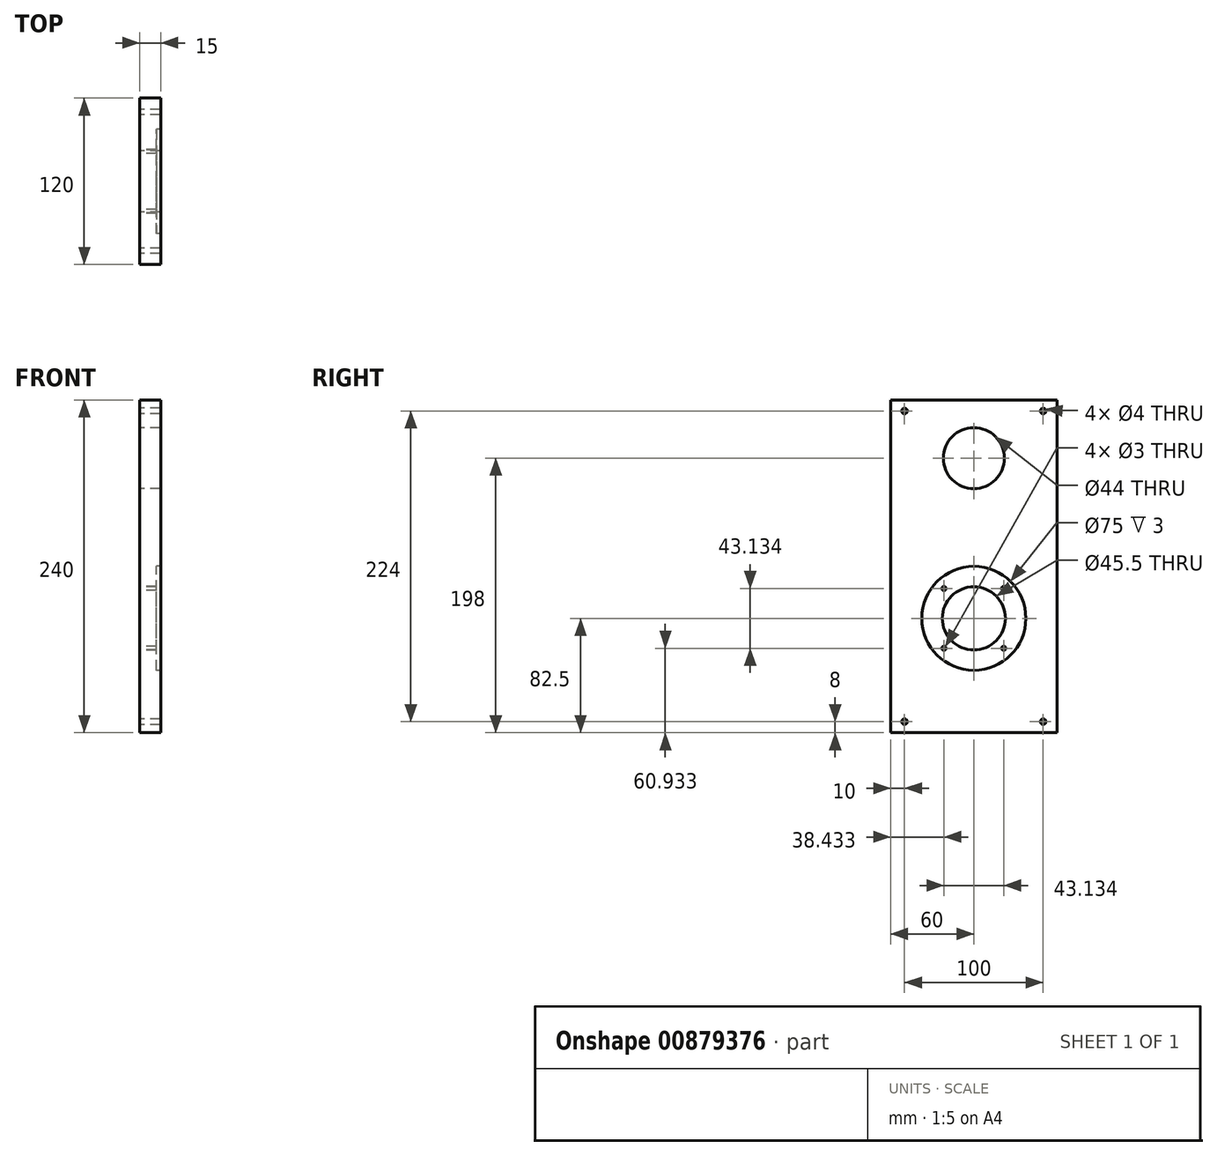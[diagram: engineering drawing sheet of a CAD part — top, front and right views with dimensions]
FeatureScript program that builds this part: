
annotation { "Feature Type Name" : "Feature", "Feature Type Description" : "" }
export const myFeature = defineFeature(function(context is Context, id is Id, definition is map)
    precondition{}
    {
        {
            var Q0;
            Q0=qCreatedBy(makeId("Right.planeOp"),FACE);
            var sketch = newSketch(context, id + "F0", { "sketchPlane" : qUnion([Q0])});
            skLineSegment(sketch, "E0.bottom", {"start": v(-60, 125) * mm, "end": v(60, 125) * mm});
            skLineSegment(sketch, "E0.top", {"start": v(-60, -115) * mm, "end": v(60, -115) * mm});
            skPoint(sketch, "E1", {"position": v(0, -32.5) * mm});
            skCircle(sketch, "E2", {"center": v(0, 83) * mm, "radius": 22 * mm});
            skCircle(sketch, "E3", {"center": v(0, 83) * mm, "radius": 16.5 * mm});
            skCircle(sketch, "E4", {"center": v(0, -32.5) * mm, "radius": 22.75 * mm});
            skCircle(sketch, "E5", {"center": v(0, -32.5) * mm, "radius": 37.5 * mm});
            skCircle(sketch, "E6", {"center": v(-21.57, -10.93) * mm, "radius": 1.5 * mm});
            skCircle(sketch, "E7.1.0", {"center": v(-21.57, -54.07) * mm, "radius": 1.5 * mm});
            skCircle(sketch, "E7.2.0", {"center": v(21.57, -54.07) * mm, "radius": 1.5 * mm});
            skCircle(sketch, "E7.3.0", {"center": v(21.57, -10.93) * mm, "radius": 1.5 * mm});
            skLineSegment(sketch, "E8", {"start": v(-60, 125) * mm, "end": v(-60, -115) * mm});
            skLineSegment(sketch, "E9", {"start": v(60, 125) * mm, "end": v(60, -115) * mm});
            skPoint(sketch, "E10.orphan", {"position": v(0, 125) * mm});
            skPoint(sketch, "E11.trimOffspring.end.orphan", {"position": v(0, -115) * mm});
            skCircle(sketch, "E12.0.1.0", {"center": v(-50, 117) * mm, "radius": 2 * mm});
            skCircle(sketch, "E13.0.1.0", {"center": v(50, 117) * mm, "radius": 2 * mm});
            skCircle(sketch, "E14.0.1.0", {"center": v(50, -107) * mm, "radius": 2 * mm});
            skCircle(sketch, "E15.0.1.0", {"center": v(-50, -107) * mm, "radius": 2 * mm});
            skSolve(sketch);
        }
        {
            var Q0;
            Q0=makeQuery(id+"F0.imprint","IMPRINT",FACE,{"disambiguationData":[TD([[makeQuery(id+"F0.imprint","IMPRINT",EDGE,{"derivedFrom":sQuery(id+"F0.wireOp",EDGE,"E5")}),-1.0]])]});
            extrude(context, id + "F1", {"entities" : qUnion([Q0]), "depth" : 15 * mm, "offsetDistance" : 25 * mm});
        }
        {
            var Q0;
            Q0=makeQuery(id+"F0.imprint","IMPRINT",FACE,{"disambiguationData":[TD([[makeQuery(id+"F0.imprint","IMPRINT",EDGE,{"derivedFrom":sQuery(id+"F0.wireOp",EDGE,"E2")}),1.0]])]});
            var Q1;
            Q1=makeQuery(id+"F0.imprint","IMPRINT",FACE,{"disambiguationData":[TD([[makeQuery(id+"F0.imprint","IMPRINT",EDGE,{"derivedFrom":sQuery(id+"F0.wireOp",EDGE,"E4")}),-1.0]])]});
            extrude(context, id + "F2", {"entities" : qUnion([Q0, Q1]), "operationType" : NewBodyOperationType.ADD, "depth" : 12 * mm, "offsetDistance" : 25 * mm});
        }
    });
